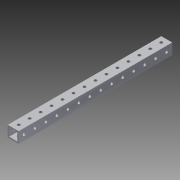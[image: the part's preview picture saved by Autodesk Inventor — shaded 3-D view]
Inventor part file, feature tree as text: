
AUTODESK INVENTOR PART (.ipt)
format: ipt  version: 2014 SP1 (Build 180222100, 222)  size: 168,448 bytes
history: native  units: in
note: dims shown in document units (in); Inventor stores cm internally (conversion verified against a paired STEP export)
features: extrude x3, sketch x3
ambient origin geometry x8: Origin, YZ Plane, XZ Plane, XY Plane, X Axis, Y Axis, Z Axis, Center Point
bodies: Solid1 (feature_tree)
feature tree (6):
  extrude  "Extrusion1"  Depth=1.0in
  extrude  "Extrusion2"  Depth=14.0in TaperAngle=0.0deg
  extrude  "Extrusion3"  Depth=1.0in
  sketch  "Sketch1"  dims[d0=1.0in d1=1.0in]
  sketch  "Sketch2"  dims[d2=0.125in d3=14.0in d4=0.0in]
  sketch  "Sketch3"  dims[d5=0.5in d7=0.26in d8=16.5in d9=0.0in d10=14.0in d11=5.5118in d13=1.0in d14=0.3937in d16=1.0in d19=0.5in d20=0.26in d21=0.26in d22=0.5in d23=0.26in d25=0.5in d26=5.5118in d28=1.0in d29=0.3937in d31=1.0in d34=1.0in d35=0.0in]
